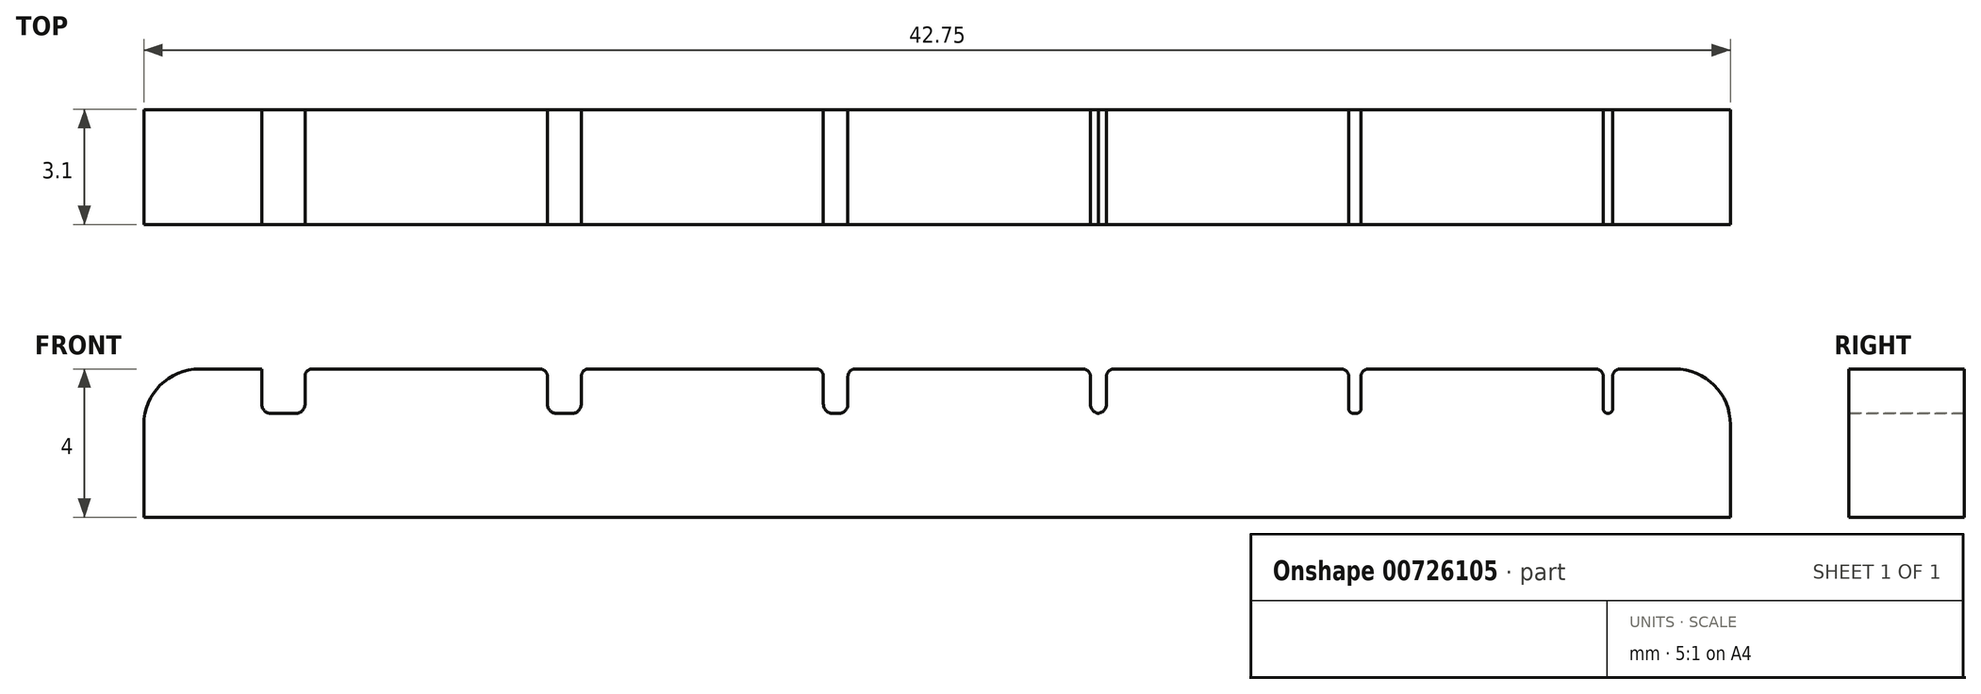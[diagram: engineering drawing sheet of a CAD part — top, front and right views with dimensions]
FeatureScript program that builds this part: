
annotation { "Feature Type Name" : "Feature", "Feature Type Description" : "" }
export const myFeature = defineFeature(function(context is Context, id is Id, definition is map)
    precondition{}
    {
        {
            var Q0;
            Q0=qCreatedBy(makeId("Top.planeOp"),FACE);
            var sketch = newSketch(context, id + "F0", { "sketchPlane" : qUnion([Q0])});
            skLineSegment(sketch, "E0.bottom", {"start": v(-13.2, -1.01) * mm, "end": v(29.55, -1.01) * mm});
            skLineSegment(sketch, "E0.top", {"start": v(-13.2, -4.11) * mm, "end": v(29.55, -4.11) * mm});
            skLineSegment(sketch, "E0.left", {"start": v(-13.2, -1.01) * mm, "end": v(-13.2, -4.11) * mm});
            skLineSegment(sketch, "E0.right", {"start": v(29.55, -1.01) * mm, "end": v(29.55, -4.11) * mm});
            skLineSegment(sketch, "E1.bottom", {"start": v(-10.02, -1.01) * mm, "end": v(-8.86, -1.01) * mm});
            skLineSegment(sketch, "E1.top", {"start": v(-10.02, -4.11) * mm, "end": v(-8.86, -4.11) * mm});
            skLineSegment(sketch, "E1.left", {"start": v(-10.02, -1.01) * mm, "end": v(-10.02, -4.11) * mm});
            skLineSegment(sketch, "E1.right", {"start": v(-8.86, -1.01) * mm, "end": v(-8.86, -4.11) * mm});
            skLineSegment(sketch, "E2", {"start": v(-9.44, -1.01) * mm, "end": v(-9.44, -4.11) * mm, "construction": true});
            skLineSegment(sketch, "E3.bottom", {"start": v(-2.33, -1.01) * mm, "end": v(-1.41, -1.01) * mm});
            skLineSegment(sketch, "E3.top", {"start": v(-2.33, -4.11) * mm, "end": v(-1.41, -4.11) * mm});
            skLineSegment(sketch, "E3.left", {"start": v(-2.33, -1.01) * mm, "end": v(-2.33, -4.11) * mm});
            skLineSegment(sketch, "E3.right", {"start": v(-1.41, -1.01) * mm, "end": v(-1.41, -4.11) * mm});
            skLineSegment(sketch, "E4", {"start": v(-1.87, -1.01) * mm, "end": v(-1.87, -4.11) * mm, "construction": true});
            skLineSegment(sketch, "E5", {"start": v(5.44, -1.01) * mm, "end": v(5.44, -4.11) * mm, "construction": true});
            skLineSegment(sketch, "E6", {"start": v(12.52, -1.01) * mm, "end": v(12.52, -4.11) * mm, "construction": true});
            skLineSegment(sketch, "E7", {"start": v(19.43, -1.01) * mm, "end": v(19.43, -4.11) * mm, "construction": true});
            skLineSegment(sketch, "E8", {"start": v(26.25, -1.01) * mm, "end": v(26.25, -4.11) * mm, "construction": true});
            skLineSegment(sketch, "E9.bottom", {"start": v(5.11, -1.01) * mm, "end": v(5.77, -1.01) * mm});
            skLineSegment(sketch, "E9.top", {"start": v(5.11, -4.11) * mm, "end": v(5.77, -4.11) * mm});
            skLineSegment(sketch, "E9.left", {"start": v(5.11, -1.01) * mm, "end": v(5.11, -4.11) * mm});
            skLineSegment(sketch, "E9.right", {"start": v(5.77, -1.01) * mm, "end": v(5.77, -4.11) * mm});
            skPoint(sketch, "E9.middle", {"position": v(5.44, -2.56) * mm});
            skLineSegment(sketch, "E10.bottom", {"start": v(12.3, -1.01) * mm, "end": v(12.74, -1.01) * mm});
            skLineSegment(sketch, "E10.top", {"start": v(12.3, -4.11) * mm, "end": v(12.74, -4.11) * mm});
            skLineSegment(sketch, "E10.left", {"start": v(12.3, -1.01) * mm, "end": v(12.3, -4.11) * mm});
            skLineSegment(sketch, "E10.right", {"start": v(12.74, -1.01) * mm, "end": v(12.74, -4.11) * mm});
            skPoint(sketch, "E10.middle", {"position": v(12.52, -2.56) * mm});
            skLineSegment(sketch, "E11.bottom", {"start": v(19.27, -1.01) * mm, "end": v(19.6, -1.01) * mm});
            skLineSegment(sketch, "E11.top", {"start": v(19.27, -4.11) * mm, "end": v(19.6, -4.11) * mm});
            skLineSegment(sketch, "E11.left", {"start": v(19.27, -1.01) * mm, "end": v(19.27, -4.11) * mm});
            skLineSegment(sketch, "E11.right", {"start": v(19.6, -1.01) * mm, "end": v(19.6, -4.11) * mm});
            skPoint(sketch, "E11.middle", {"position": v(19.43, -2.56) * mm});
            skLineSegment(sketch, "E12.bottom", {"start": v(26.12, -1.01) * mm, "end": v(26.38, -1.01) * mm});
            skLineSegment(sketch, "E12.top", {"start": v(26.12, -4.11) * mm, "end": v(26.38, -4.11) * mm});
            skLineSegment(sketch, "E12.left", {"start": v(26.12, -1.01) * mm, "end": v(26.12, -4.11) * mm});
            skLineSegment(sketch, "E12.right", {"start": v(26.38, -1.01) * mm, "end": v(26.38, -4.11) * mm});
            skPoint(sketch, "E12.middle", {"position": v(26.25, -2.56) * mm});
            skSolve(sketch);
        }
        {
            var Q0;
            Q0 = qSketchRegion(id + "F0", true);
            extrude(context, id + "F1", {"entities" : qUnion([Q0]), "depth" : 4 * mm, "offsetDistance" : 25 * mm});
        }
        {
            var Q0;
            Q0=makeQuery(id+"F1.opExtrude","CAP_FACE",FACE,{"disambiguationData":[OSD([sQuery(id+"F0.wireOp",EDGE,"E0.bottom"),sQuery(id+"F0.wireOp",EDGE,"E0.top"),sQuery(id+"F0.wireOp",EDGE,"E0.left"),sQuery(id+"F0.wireOp",EDGE,"E0.right"),sQuery(id+"F0.wireOp",EDGE,"E1.bottom"),sQuery(id+"F0.wireOp",EDGE,"E1.top"),sQuery(id+"F0.wireOp",EDGE,"E3.bottom"),sQuery(id+"F0.wireOp",EDGE,"E3.top"),sQuery(id+"F0.wireOp",EDGE,"E9.bottom"),sQuery(id+"F0.wireOp",EDGE,"E9.top"),sQuery(id+"F0.wireOp",EDGE,"E10.bottom"),sQuery(id+"F0.wireOp",EDGE,"E10.top"),sQuery(id+"F0.wireOp",EDGE,"E11.bottom"),sQuery(id+"F0.wireOp",EDGE,"E11.top"),sQuery(id+"F0.wireOp",EDGE,"E12.bottom"),sQuery(id+"F0.wireOp",EDGE,"E12.top")])],"isStart":false});
            var sketch = newSketch(context, id + "F2", { "sketchPlane" : qUnion([Q0])});
            skLineSegment(sketch, "E13.0", {"start": v(-10.02, -1.01) * mm, "end": v(-10.02, -4.11) * mm});
            skLineSegment(sketch, "E13.1", {"start": v(-10.02, -4.11) * mm, "end": v(-8.86, -4.11) * mm});
            skLineSegment(sketch, "E13.2", {"start": v(-10.02, -1.01) * mm, "end": v(-8.86, -1.01) * mm});
            skLineSegment(sketch, "E13.3", {"start": v(-9.44, -1.01) * mm, "end": v(-9.44, -4.11) * mm});
            skLineSegment(sketch, "E13.4", {"start": v(-8.86, -1.01) * mm, "end": v(-8.86, -4.11) * mm});
            skLineSegment(sketch, "E14.0", {"start": v(-1.41, -1.01) * mm, "end": v(-1.41, -4.11) * mm});
            skLineSegment(sketch, "E14.1", {"start": v(-2.33, -4.11) * mm, "end": v(-1.41, -4.11) * mm});
            skLineSegment(sketch, "E14.2", {"start": v(-2.33, -1.01) * mm, "end": v(-2.33, -4.11) * mm});
            skLineSegment(sketch, "E14.3", {"start": v(-2.33, -1.01) * mm, "end": v(-1.41, -1.01) * mm});
            skLineSegment(sketch, "E14.4", {"start": v(-1.87, -1.01) * mm, "end": v(-1.87, -4.11) * mm});
            skLineSegment(sketch, "E15.0", {"start": v(5.11, -1.01) * mm, "end": v(5.11, -4.11) * mm});
            skLineSegment(sketch, "E15.1", {"start": v(5.11, -4.11) * mm, "end": v(5.77, -4.11) * mm});
            skLineSegment(sketch, "E15.2", {"start": v(5.77, -1.01) * mm, "end": v(5.77, -4.11) * mm});
            skLineSegment(sketch, "E15.3", {"start": v(5.44, -1.01) * mm, "end": v(5.44, -4.11) * mm});
            skLineSegment(sketch, "E15.4", {"start": v(5.11, -1.01) * mm, "end": v(5.77, -1.01) * mm});
            skLineSegment(sketch, "E16.0", {"start": v(12.3, -4.11) * mm, "end": v(12.74, -4.11) * mm});
            skLineSegment(sketch, "E16.1", {"start": v(12.52, -1.01) * mm, "end": v(12.52, -4.11) * mm});
            skLineSegment(sketch, "E16.2", {"start": v(12.74, -1.01) * mm, "end": v(12.74, -4.11) * mm});
            skLineSegment(sketch, "E16.3", {"start": v(12.3, -1.01) * mm, "end": v(12.3, -4.11) * mm});
            skLineSegment(sketch, "E16.4", {"start": v(12.3, -1.01) * mm, "end": v(12.74, -1.01) * mm});
            skLineSegment(sketch, "E17.0", {"start": v(19.6, -1.01) * mm, "end": v(19.6, -4.11) * mm});
            skLineSegment(sketch, "E17.1", {"start": v(19.27, -4.11) * mm, "end": v(19.6, -4.11) * mm});
            skLineSegment(sketch, "E17.2", {"start": v(19.43, -1.01) * mm, "end": v(19.43, -4.11) * mm});
            skLineSegment(sketch, "E17.3", {"start": v(19.27, -1.01) * mm, "end": v(19.6, -1.01) * mm});
            skLineSegment(sketch, "E17.4", {"start": v(19.27, -1.01) * mm, "end": v(19.27, -4.11) * mm});
            skLineSegment(sketch, "E18.0", {"start": v(26.12, -1.01) * mm, "end": v(26.12, -4.11) * mm});
            skLineSegment(sketch, "E18.1", {"start": v(26.25, -1.01) * mm, "end": v(26.25, -4.11) * mm});
            skLineSegment(sketch, "E18.2", {"start": v(26.38, -1.01) * mm, "end": v(26.38, -4.11) * mm});
            skLineSegment(sketch, "E18.3", {"start": v(26.12, -1.01) * mm, "end": v(26.38, -1.01) * mm});
            skSolve(sketch);
        }
        {
            var Q0;
            {var subQ2=sQuery(id+"F2.wireOp",EDGE,"E13.3");Q0=makeQuery(id+"F2.imprint","IMPRINT",FACE,{"disambiguationData":[TD([[makeQuery(id+"F2.imprint","IMPRINT",EDGE,{"derivedFrom":subQ2}),1.0]])]});}
            var Q1;
            {var subQ0=sQuery(id+"F2.wireOp",EDGE,"E13.0");Q1=makeQuery(id+"F2.imprint","IMPRINT",FACE,{"disambiguationData":[TD([[makeQuery(id+"F2.imprint","IMPRINT",EDGE,{"derivedFrom":subQ0}),1.0]])]});}
            var Q2;
            {var subQ0=sQuery(id+"F2.wireOp",EDGE,"E14.0");Q2=makeQuery(id+"F2.imprint","IMPRINT",FACE,{"disambiguationData":[TD([[makeQuery(id+"F2.imprint","IMPRINT",EDGE,{"derivedFrom":subQ0}),-1.0]])]});}
            var Q3;
            {var subQ0=sQuery(id+"F2.wireOp",EDGE,"E14.2");Q3=makeQuery(id+"F2.imprint","IMPRINT",FACE,{"disambiguationData":[TD([[makeQuery(id+"F2.imprint","IMPRINT",EDGE,{"derivedFrom":subQ0}),1.0]])]});}
            var Q4;
            {var subQ0=sQuery(id+"F2.wireOp",EDGE,"E15.0");Q4=makeQuery(id+"F2.imprint","IMPRINT",FACE,{"disambiguationData":[TD([[makeQuery(id+"F2.imprint","IMPRINT",EDGE,{"derivedFrom":subQ0}),1.0]])]});}
            var Q5;
            {var subQ0=sQuery(id+"F2.wireOp",EDGE,"E15.2");Q5=makeQuery(id+"F2.imprint","IMPRINT",FACE,{"disambiguationData":[TD([[makeQuery(id+"F2.imprint","IMPRINT",EDGE,{"derivedFrom":subQ0}),-1.0]])]});}
            var Q6;
            {var subQ2=sQuery(id+"F2.wireOp",EDGE,"E16.1");Q6=makeQuery(id+"F2.imprint","IMPRINT",FACE,{"disambiguationData":[TD([[makeQuery(id+"F2.imprint","IMPRINT",EDGE,{"derivedFrom":subQ2}),-1.0]])]});}
            var Q7;
            {var subQ2=sQuery(id+"F2.wireOp",EDGE,"E16.1");Q7=makeQuery(id+"F2.imprint","IMPRINT",FACE,{"disambiguationData":[TD([[makeQuery(id+"F2.imprint","IMPRINT",EDGE,{"derivedFrom":subQ2}),1.0]])]});}
            var Q8;
            {var subQ2=sQuery(id+"F2.wireOp",EDGE,"E17.2");Q8=makeQuery(id+"F2.imprint","IMPRINT",FACE,{"disambiguationData":[TD([[makeQuery(id+"F2.imprint","IMPRINT",EDGE,{"derivedFrom":subQ2}),-1.0]])]});}
            var Q9;
            {var subQ0=sQuery(id+"F2.wireOp",EDGE,"E17.0");Q9=makeQuery(id+"F2.imprint","IMPRINT",FACE,{"disambiguationData":[TD([[makeQuery(id+"F2.imprint","IMPRINT",EDGE,{"derivedFrom":subQ0}),-1.0]])]});}
            var Q10;
            {var subQ0=sQuery(id+"F2.wireOp",EDGE,"E18.1");Q10=makeQuery(id+"F2.imprint","IMPRINT",FACE,{"disambiguationData":[TD([[makeQuery(id+"F2.imprint","IMPRINT",EDGE,{"derivedFrom":subQ0}),1.0]])]});}
            var Q11;
            {var subQ0=sQuery(id+"F2.wireOp",EDGE,"E18.0");Q11=makeQuery(id+"F2.imprint","IMPRINT",FACE,{"disambiguationData":[TD([[makeQuery(id+"F2.imprint","IMPRINT",EDGE,{"derivedFrom":subQ0}),1.0]])]});}
            extrude(context, id + "F3", {"entities" : qUnion([Q0, Q1, Q2, Q3, Q4, Q5, Q6, Q7, Q8, Q9, Q10, Q11]), "operationType" : NewBodyOperationType.REMOVE, "oppositeDirection" : true, "depth" : 1.2 * mm, "offsetDistance" : 25 * mm});
        }
        {
            var Q0;
            Q0=makeQuery(id+"F3.boolean.opBoolean","COPY",EDGE,{"derivedFrom":makeQuery(id+"F3.opExtrude","CAP_EDGE",EDGE,{"disambiguationData":[OSD([sQuery(id+"F2.wireOp",EDGE,"E13.0")])],"isStart":false})});
            var Q1;
            Q1=makeQuery(id+"F3.boolean.opBoolean","COPY",EDGE,{"derivedFrom":makeQuery(id+"F3.opExtrude","CAP_EDGE",EDGE,{"disambiguationData":[OSD([sQuery(id+"F2.wireOp",EDGE,"E13.4")])],"isStart":false})});
            var Q2;
            Q2=makeQuery(id+"F3.boolean.opBoolean","COPY",EDGE,{"derivedFrom":makeQuery(id+"F3.opExtrude","CAP_EDGE",EDGE,{"disambiguationData":[OSD([sQuery(id+"F2.wireOp",EDGE,"E14.0")])],"isStart":false})});
            var Q3;
            Q3=makeQuery(id+"F3.boolean.opBoolean","COPY",EDGE,{"derivedFrom":makeQuery(id+"F3.opExtrude","CAP_EDGE",EDGE,{"disambiguationData":[OSD([sQuery(id+"F2.wireOp",EDGE,"E14.2")])],"isStart":false})});
            var Q4;
            Q4=makeQuery(id+"F3.boolean.opBoolean","COPY",EDGE,{"derivedFrom":makeQuery(id+"F3.opExtrude","CAP_EDGE",EDGE,{"disambiguationData":[OSD([sQuery(id+"F2.wireOp",EDGE,"E15.0")])],"isStart":false})});
            var Q5;
            Q5=makeQuery(id+"F3.boolean.opBoolean","COPY",EDGE,{"derivedFrom":makeQuery(id+"F3.opExtrude","CAP_EDGE",EDGE,{"disambiguationData":[OSD([sQuery(id+"F2.wireOp",EDGE,"E15.2")])],"isStart":false})});
            var Q6;
            Q6=makeQuery(id+"F3.boolean.opBoolean","COPY",EDGE,{"derivedFrom":makeQuery(id+"F3.opExtrude","CAP_EDGE",EDGE,{"disambiguationData":[OSD([sQuery(id+"F2.wireOp",EDGE,"E16.2")])],"isStart":false})});
            var Q7;
            Q7=makeQuery(id+"F3.boolean.opBoolean","COPY",EDGE,{"derivedFrom":makeQuery(id+"F3.opExtrude","CAP_EDGE",EDGE,{"disambiguationData":[OSD([sQuery(id+"F2.wireOp",EDGE,"E16.3")])],"isStart":false})});
            fillet(context, id + "F4", {"entities" : qUnion([Q0, Q1, Q2, Q3, Q4, Q5, Q6, Q7]), "radius" : .25 * mm, "tangentPropagation" : true, "allowEdgeOverflow" : false});
        }
        {
            var Q0;
            Q0=makeQuery(id+"F3.boolean.opBoolean","COPY",EDGE,{"derivedFrom":makeQuery(id+"F3.opExtrude","CAP_EDGE",EDGE,{"disambiguationData":[OSD([sQuery(id+"F2.wireOp",EDGE,"E17.4")])],"isStart":false})});
            var Q1;
            Q1=makeQuery(id+"F3.boolean.opBoolean","COPY",EDGE,{"derivedFrom":makeQuery(id+"F3.opExtrude","CAP_EDGE",EDGE,{"disambiguationData":[OSD([sQuery(id+"F2.wireOp",EDGE,"E17.0")])],"isStart":false})});
            var Q2;
            Q2=makeQuery(id+"F3.boolean.opBoolean","COPY",EDGE,{"derivedFrom":makeQuery(id+"F3.opExtrude","CAP_EDGE",EDGE,{"disambiguationData":[OSD([sQuery(id+"F2.wireOp",EDGE,"E18.2")])],"isStart":false})});
            var Q3;
            Q3=makeQuery(id+"F3.boolean.opBoolean","COPY",EDGE,{"derivedFrom":makeQuery(id+"F3.opExtrude","CAP_EDGE",EDGE,{"disambiguationData":[OSD([sQuery(id+"F2.wireOp",EDGE,"E18.0")])],"isStart":false})});
            fillet(context, id + "F5", {"entities" : qUnion([Q0, Q1, Q2, Q3]), "radius" : .125 * mm, "tangentPropagation" : true, "allowEdgeOverflow" : false});
        }
        {
            var Q0;
            Q0=makeQuery(id+"F1.opExtrude","CAP_EDGE",EDGE,{"disambiguationData":[OSD([sQuery(id+"F0.wireOp",EDGE,"E0.right")])],"isStart":false});
            var Q1;
            Q1=makeQuery(id+"F1.opExtrude","CAP_EDGE",EDGE,{"disambiguationData":[OSD([sQuery(id+"F0.wireOp",EDGE,"E0.left")])],"isStart":false});
            fillet(context, id + "F6", {"entities" : qUnion([Q0, Q1]), "radius" : 1.5 * mm, "tangentPropagation" : true, "allowEdgeOverflow" : false});
        }
        {
            var Q0;
            Q0=makeQuery(id+"F3.boolean.opBoolean","COPY",EDGE,{"derivedFrom":makeQuery(id+"F3.opExtrude","CAP_EDGE",EDGE,{"disambiguationData":[OSD([sQuery(id+"F2.wireOp",EDGE,"E13.0")])],"isStart":true})});
            var Q1;
            Q1=makeQuery(id+"F3.boolean.opBoolean","COPY",EDGE,{"derivedFrom":makeQuery(id+"F3.opExtrude","CAP_EDGE",EDGE,{"disambiguationData":[OSD([sQuery(id+"F2.wireOp",EDGE,"E13.4")])],"isStart":true})});
            var Q2;
            Q2=makeQuery(id+"F3.boolean.opBoolean","COPY",EDGE,{"derivedFrom":makeQuery(id+"F3.opExtrude","CAP_EDGE",EDGE,{"disambiguationData":[OSD([sQuery(id+"F2.wireOp",EDGE,"E14.2")])],"isStart":true})});
            var Q3;
            Q3=makeQuery(id+"F3.boolean.opBoolean","COPY",EDGE,{"derivedFrom":makeQuery(id+"F3.opExtrude","CAP_EDGE",EDGE,{"disambiguationData":[OSD([sQuery(id+"F2.wireOp",EDGE,"E14.0")])],"isStart":true})});
            var Q4;
            Q4=makeQuery(id+"F3.boolean.opBoolean","COPY",EDGE,{"derivedFrom":makeQuery(id+"F3.opExtrude","CAP_EDGE",EDGE,{"disambiguationData":[OSD([sQuery(id+"F2.wireOp",EDGE,"E15.0")])],"isStart":true})});
            var Q5;
            Q5=makeQuery(id+"F3.boolean.opBoolean","COPY",EDGE,{"derivedFrom":makeQuery(id+"F3.opExtrude","CAP_EDGE",EDGE,{"disambiguationData":[OSD([sQuery(id+"F2.wireOp",EDGE,"E15.2")])],"isStart":true})});
            var Q6;
            Q6=makeQuery(id+"F3.boolean.opBoolean","COPY",EDGE,{"derivedFrom":makeQuery(id+"F3.opExtrude","CAP_EDGE",EDGE,{"disambiguationData":[OSD([sQuery(id+"F2.wireOp",EDGE,"E16.3")])],"isStart":true})});
            var Q7;
            Q7=makeQuery(id+"F3.boolean.opBoolean","COPY",EDGE,{"derivedFrom":makeQuery(id+"F3.opExtrude","CAP_EDGE",EDGE,{"disambiguationData":[OSD([sQuery(id+"F2.wireOp",EDGE,"E16.2")])],"isStart":true})});
            var Q8;
            Q8=makeQuery(id+"F3.boolean.opBoolean","COPY",EDGE,{"derivedFrom":makeQuery(id+"F3.opExtrude","CAP_EDGE",EDGE,{"disambiguationData":[OSD([sQuery(id+"F2.wireOp",EDGE,"E17.4")])],"isStart":true})});
            var Q9;
            Q9=makeQuery(id+"F3.boolean.opBoolean","COPY",EDGE,{"derivedFrom":makeQuery(id+"F3.opExtrude","CAP_EDGE",EDGE,{"disambiguationData":[OSD([sQuery(id+"F2.wireOp",EDGE,"E17.0")])],"isStart":true})});
            var Q10;
            Q10=makeQuery(id+"F3.boolean.opBoolean","COPY",EDGE,{"derivedFrom":makeQuery(id+"F3.opExtrude","CAP_EDGE",EDGE,{"disambiguationData":[OSD([sQuery(id+"F2.wireOp",EDGE,"E18.0")])],"isStart":true})});
            var Q11;
            Q11=makeQuery(id+"F3.boolean.opBoolean","COPY",EDGE,{"derivedFrom":makeQuery(id+"F3.opExtrude","CAP_EDGE",EDGE,{"disambiguationData":[OSD([sQuery(id+"F2.wireOp",EDGE,"E18.2")])],"isStart":true})});
            fillet(context, id + "F7", {"entities" : qUnion([Q0, Q1, Q2, Q3, Q4, Q5, Q6, Q7, Q8, Q9, Q10, Q11]), "radius" : .2 * mm, "tangentPropagation" : true, "allowEdgeOverflow" : false});
        }
    });
